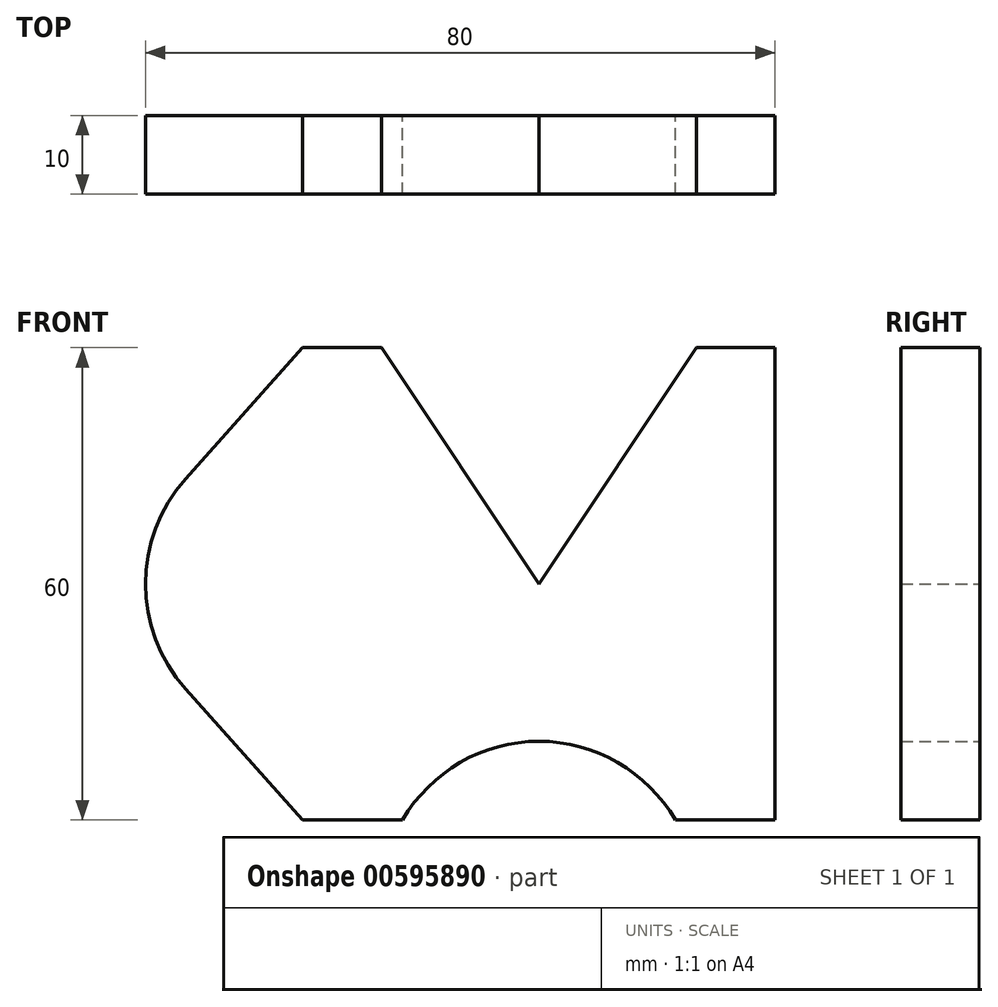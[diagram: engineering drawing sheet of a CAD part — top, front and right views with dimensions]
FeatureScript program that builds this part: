
annotation { "Feature Type Name" : "Feature", "Feature Type Description" : "" }
export const myFeature = defineFeature(function(context is Context, id is Id, definition is map)
    precondition{}
    {
        {
            var Q0;
            Q0=qCreatedBy(makeId("Front.planeOp"),FACE);
            var sketch = newSketch(context, id + "F0", { "sketchPlane" : qUnion([Q0])});
            skLineSegment(sketch, "E0", {"start": v(20, 30) * mm, "end": v(30, 30) * mm});
            skLineSegment(sketch, "E1", {"start": v(30, 30) * mm, "end": v(30, -30) * mm});
            skLineSegment(sketch, "E2", {"start": v(30, -30) * mm, "end": v(17.32, -30) * mm});
            skArc(sketch, "E3", {"start": v(17.32, -30) * mm, "mid": v(0, -20) * mm, "end": v(-17.32, -30) * mm});
            skLineSegment(sketch, "E4", {"start": v(-17.32, -30) * mm, "end": v(-30, -30) * mm});
            skLineSegment(sketch, "E5", {"start": v(-30, 30) * mm, "end": v(-20, 30) * mm});
            skLineSegment(sketch, "E6", {"start": v(-20, 30) * mm, "end": v(0, 0) * mm});
            skLineSegment(sketch, "E7", {"start": v(0, 0) * mm, "end": v(20, 30) * mm});
            skLineSegment(sketch, "E8", {"start": v(-30, -30) * mm, "end": v(-44.9, -13.33) * mm});
            skLineSegment(sketch, "E9", {"start": v(-30, 30) * mm, "end": v(-44.9, 13.33) * mm});
            skArc(sketch, "E10", {"start": v(-44.9, 13.33) * mm, "mid": v(-50, 0) * mm, "end": v(-44.9, -13.33) * mm});
            skSolve(sketch);
        }
        {
            var Q0;
            Q0 = qSketchRegion(id + "F0", true);
            extrude(context, id + "F1", {"entities" : qUnion([Q0]), "depth" : 10 * mm, "offsetDistance" : 25 * mm});
        }
    });
